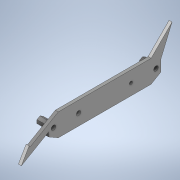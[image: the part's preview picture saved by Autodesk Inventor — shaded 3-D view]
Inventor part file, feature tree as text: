
AUTODESK INVENTOR PART (.ipt)
format: ipt  version: 2020 (Build 240168000, 168)  size: 174,080 bytes
history: native  units: in
note: dims shown in document units (in); Inventor stores cm internally (conversion verified against a paired STEP export)
features: other x3, extrude x2, sketch x2
ambient origin geometry x8: Origin, YZ Plane, XZ Plane, XY Plane, X Axis, Y Axis, Z Axis, Center Point
bodies: Solid1 (feature_tree)
feature tree (7):
  other  "HexWheelGuard.ipt"
  extrude  "Extrusion1"  Depth=0.315in
  extrude  "Extrusion2"  Depth=0.3937in
  other  "Solid1::HexWheelGuard.ipt"
  other  "TaggingFeature2"
  sketch  "Sketch1"  dims[d1=0.3937in d2=0.315in]
  sketch  "Sketch2"  dims[d3=60.0deg d4=1.4843in d5=0.0787in d6=0.3937in d7=0.0in d10=0.5906in d11=1.1024in d12=0.3937in d13=0.0in]
